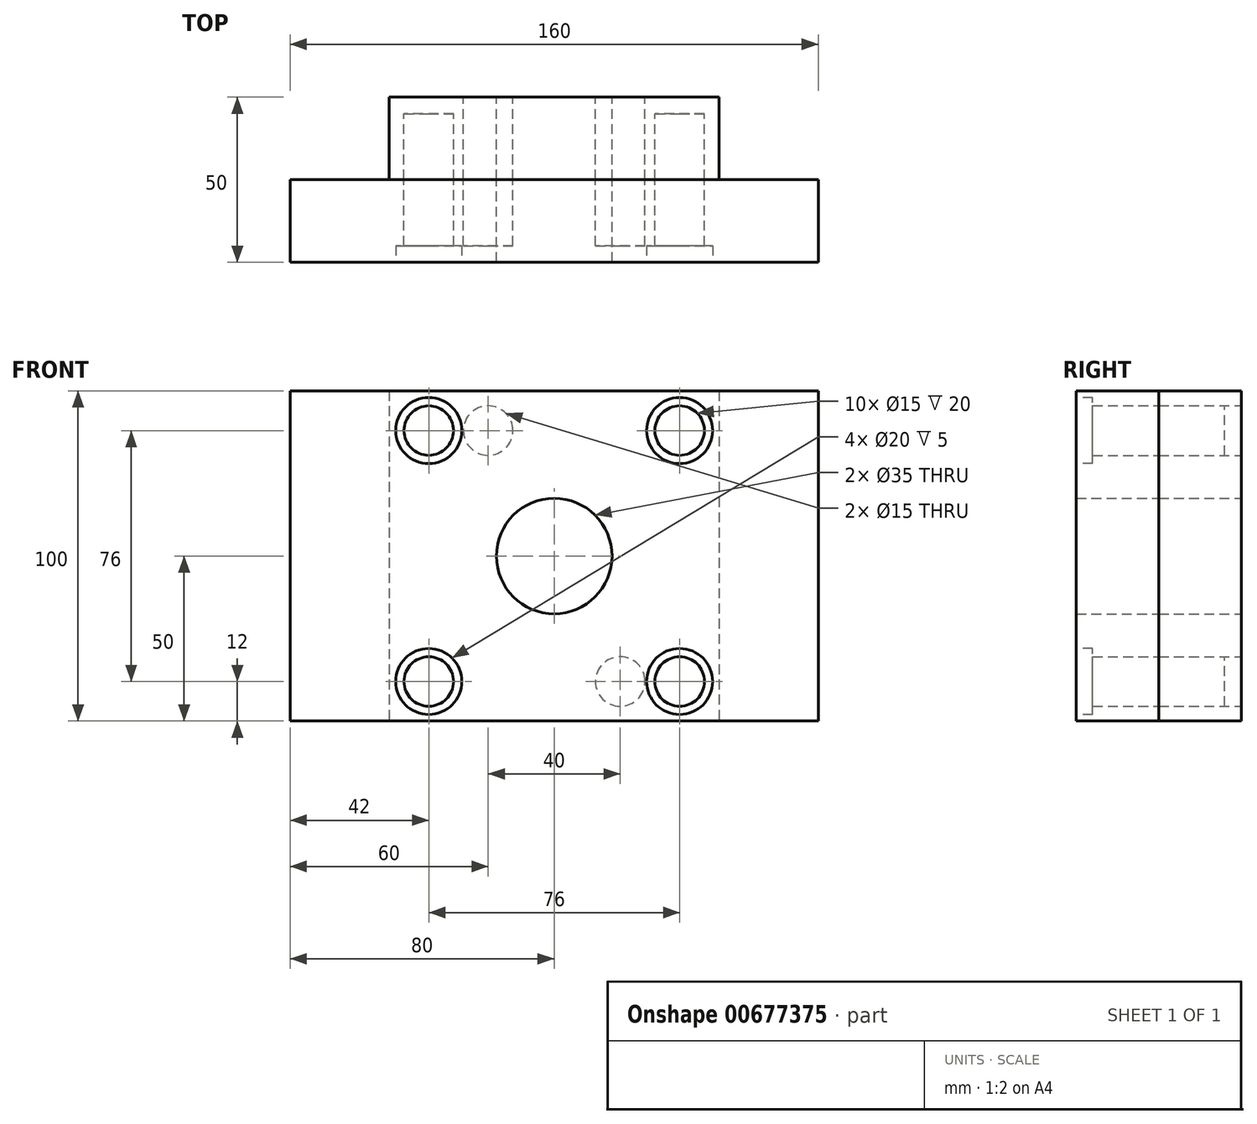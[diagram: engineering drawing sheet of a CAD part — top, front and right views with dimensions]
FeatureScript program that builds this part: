
annotation { "Feature Type Name" : "Feature", "Feature Type Description" : "" }
export const myFeature = defineFeature(function(context is Context, id is Id, definition is map)
    precondition{}
    {
        {
            var Q0;
            Q0=qCreatedBy(makeId("Front.planeOp"),FACE);
            var sketch = newSketch(context, id + "F0", { "sketchPlane" : qUnion([Q0])});
            skLineSegment(sketch, "E0.bottom", {"start": v(50, 50) * mm, "end": v(-50, 50) * mm});
            skLineSegment(sketch, "E0.top", {"start": v(50, -50) * mm, "end": v(-50, -50) * mm});
            skLineSegment(sketch, "E0.left", {"start": v(50, 50) * mm, "end": v(50, -50) * mm});
            skLineSegment(sketch, "E0.right", {"start": v(-50, 50) * mm, "end": v(-50, -50) * mm});
            skPoint(sketch, "E0.middle", {"position": v(0, 0) * mm});
            skCircle(sketch, "E1", {"center": v(0, 0) * mm, "radius": 17.5 * mm});
            skCircle(sketch, "E2", {"center": v(38, 38) * mm, "radius": 7.5 * mm});
            skCircle(sketch, "E3.1.0", {"center": v(-38, 38) * mm, "radius": 7.5 * mm});
            skCircle(sketch, "E3.2.0", {"center": v(-38, -38) * mm, "radius": 7.5 * mm});
            skCircle(sketch, "E3.3.0", {"center": v(38, -38) * mm, "radius": 7.5 * mm});
            skCircle(sketch, "E4", {"center": v(20, -38) * mm, "radius": 7.5 * mm});
            skCircle(sketch, "E5", {"center": v(-20, 38) * mm, "radius": 7.5 * mm});
            skSolve(sketch);
        }
        {
            var Q0;
            Q0 = qSketchRegion(id + "F0", true);
            extrude(context, id + "F1", {"entities" : qUnion([Q0]), "depth" : 25 * mm, "offsetDistance" : 25 * mm});
        }
        {
            var Q0;
            Q0=makeQuery(id+"F1.opExtrude","CAP_FACE",FACE,{"disambiguationData":[OSD([sQuery(id+"F0.wireOp",EDGE,"E0.bottom"),sQuery(id+"F0.wireOp",EDGE,"E0.top"),sQuery(id+"F0.wireOp",EDGE,"E0.left"),sQuery(id+"F0.wireOp",EDGE,"E0.right"),sQuery(id+"F0.wireOp",EDGE,"E1"),sQuery(id+"F0.wireOp",EDGE,"E2"),sQuery(id+"F0.wireOp",EDGE,"E3.1.0"),sQuery(id+"F0.wireOp",EDGE,"E3.2.0"),sQuery(id+"F0.wireOp",EDGE,"E3.3.0"),sQuery(id+"F0.wireOp",EDGE,"E4"),sQuery(id+"F0.wireOp",EDGE,"E5")])],"isStart":false});
            var sketch = newSketch(context, id + "F2", { "sketchPlane" : qUnion([Q0])});
            skLineSegment(sketch, "E6.bottom", {"start": v(80, 50) * mm, "end": v(-80, 50) * mm});
            skLineSegment(sketch, "E6.top", {"start": v(80, -50) * mm, "end": v(-80, -50) * mm});
            skLineSegment(sketch, "E6.left", {"start": v(80, 50) * mm, "end": v(80, -50) * mm});
            skLineSegment(sketch, "E6.right", {"start": v(-80, 50) * mm, "end": v(-80, -50) * mm});
            skPoint(sketch, "E6.middle", {"position": v(0, 0) * mm});
            skCircle(sketch, "E7.0", {"center": v(-38, 38) * mm, "radius": 7.5 * mm});
            skCircle(sketch, "E8.0", {"center": v(-20, 38) * mm, "radius": 7.5 * mm});
            skCircle(sketch, "E9.0", {"center": v(38, 38) * mm, "radius": 7.5 * mm});
            skCircle(sketch, "E10.0", {"center": v(38, -38) * mm, "radius": 7.5 * mm});
            skCircle(sketch, "E11.0", {"center": v(20, -38) * mm, "radius": 7.5 * mm});
            skCircle(sketch, "E12.0", {"center": v(-38, -38) * mm, "radius": 7.5 * mm});
            skCircle(sketch, "E13.0", {"center": v(0, 0) * mm, "radius": 17.5 * mm});
            skSolve(sketch);
        }
        {
            var Q0;
            Q0 = qSketchRegion(id + "F2", true);
            extrude(context, id + "F3", {"entities" : qUnion([Q0]), "depth" : 25 * mm, "offsetDistance" : 25 * mm});
        }
        {
            var Q0;
            Q0=makeQuery(id+"F3.opExtrude","CAP_FACE",FACE,{"disambiguationData":[OSD([sQuery(id+"F2.wireOp",EDGE,"E6.bottom"),sQuery(id+"F2.wireOp",EDGE,"E6.top"),sQuery(id+"F2.wireOp",EDGE,"E6.left"),sQuery(id+"F2.wireOp",EDGE,"E6.right"),sQuery(id+"F2.wireOp",EDGE,"E7.0"),sQuery(id+"F2.wireOp",EDGE,"E8.0"),sQuery(id+"F2.wireOp",EDGE,"E9.0"),sQuery(id+"F2.wireOp",EDGE,"E10.0"),sQuery(id+"F2.wireOp",EDGE,"E11.0"),sQuery(id+"F2.wireOp",EDGE,"E12.0"),sQuery(id+"F2.wireOp",EDGE,"E13.0")])],"isStart":false});
            var sketch = newSketch(context, id + "F4", { "sketchPlane" : qUnion([Q0])});
            skCircle(sketch, "E14.0", {"center": v(-20, 38) * mm, "radius": 7.5 * mm});
            skCircle(sketch, "E15.0", {"center": v(20, -38) * mm, "radius": 7.5 * mm});
            skSolve(sketch);
        }
        {
            var Q0;
            Q0 = qSketchRegion(id + "F4", true);
            extrude(context, id + "F5", {"entities" : qUnion([Q0]), "operationType" : NewBodyOperationType.ADD, "oppositeDirection" : true, "depth" : 5 * mm, "offsetDistance" : 25 * mm});
        }
        {
            var Q0;
            Q0=makeQuery(id+"F1.opExtrude","CAP_FACE",FACE,{"disambiguationData":[OSD([sQuery(id+"F0.wireOp",EDGE,"E0.bottom"),sQuery(id+"F0.wireOp",EDGE,"E0.top"),sQuery(id+"F0.wireOp",EDGE,"E0.left"),sQuery(id+"F0.wireOp",EDGE,"E0.right"),sQuery(id+"F0.wireOp",EDGE,"E1"),sQuery(id+"F0.wireOp",EDGE,"E2"),sQuery(id+"F0.wireOp",EDGE,"E3.1.0"),sQuery(id+"F0.wireOp",EDGE,"E3.2.0"),sQuery(id+"F0.wireOp",EDGE,"E3.3.0"),sQuery(id+"F0.wireOp",EDGE,"E4"),sQuery(id+"F0.wireOp",EDGE,"E5")])],"isStart":true});
            var sketch = newSketch(context, id + "F6", { "sketchPlane" : qUnion([Q0])});
            skCircle(sketch, "E16.0", {"center": v(38, -38) * mm, "radius": 7.5 * mm});
            skCircle(sketch, "E17.0", {"center": v(-38, -38) * mm, "radius": 7.5 * mm});
            skCircle(sketch, "E18.0", {"center": v(-38, 38) * mm, "radius": 7.5 * mm});
            skCircle(sketch, "E19.0", {"center": v(38, 38) * mm, "radius": 7.5 * mm});
            skSolve(sketch);
        }
        {
            var Q0;
            Q0 = qSketchRegion(id + "F6", true);
            extrude(context, id + "F7", {"entities" : qUnion([Q0]), "operationType" : NewBodyOperationType.ADD, "oppositeDirection" : true, "depth" : 5 * mm, "offsetDistance" : 25 * mm});
        }
        {
            var Q0;
            Q0=makeQuery(id+"F5.boolean.opBoolean","MERGE",FACE,{"derivedFrom":[makeQuery(id+"F3.opExtrude","CAP_FACE",FACE,{"disambiguationData":[OSD([sQuery(id+"F2.wireOp",EDGE,"E6.bottom"),sQuery(id+"F2.wireOp",EDGE,"E6.top"),sQuery(id+"F2.wireOp",EDGE,"E6.left"),sQuery(id+"F2.wireOp",EDGE,"E6.right"),sQuery(id+"F2.wireOp",EDGE,"E7.0"),sQuery(id+"F2.wireOp",EDGE,"E8.0"),sQuery(id+"F2.wireOp",EDGE,"E9.0"),sQuery(id+"F2.wireOp",EDGE,"E10.0"),sQuery(id+"F2.wireOp",EDGE,"E11.0"),sQuery(id+"F2.wireOp",EDGE,"E12.0"),sQuery(id+"F2.wireOp",EDGE,"E13.0")])],"isStart":false}),makeQuery(id+"F5.opExtrude","CAP_FACE",FACE,{"disambiguationData":[OSD([sQuery(id+"F4.wireOp",EDGE,"E14.0")])],"isStart":true}),makeQuery(id+"F5.opExtrude","CAP_FACE",FACE,{"disambiguationData":[OSD([sQuery(id+"F4.wireOp",EDGE,"E15.0")])],"isStart":true})]});
            var sketch = newSketch(context, id + "F8", { "sketchPlane" : qUnion([Q0])});
            skCircle(sketch, "E20.0", {"center": v(38, 38) * mm, "radius": 7.5 * mm});
            skCircle(sketch, "E21.0", {"center": v(-38, 38) * mm, "radius": 7.5 * mm});
            skCircle(sketch, "E22.0", {"center": v(-38, -38) * mm, "radius": 7.5 * mm});
            skCircle(sketch, "E23.0", {"center": v(38, -38) * mm, "radius": 7.5 * mm});
            skCircle(sketch, "E24", {"center": v(38, -38) * mm, "radius": 10 * mm});
            skCircle(sketch, "E25.1.0", {"center": v(38, 38) * mm, "radius": 10 * mm});
            skCircle(sketch, "E25.2.0", {"center": v(-38, 38) * mm, "radius": 10 * mm});
            skCircle(sketch, "E25.3.0", {"center": v(-38, -38) * mm, "radius": 10 * mm});
            skPoint(sketch, "E25.center", {"position": v(0, 0) * mm});
            skSolve(sketch);
        }
        {
            var Q0;
            Q0 = qSketchRegion(id + "F8", true);
            extrude(context, id + "F9", {"entities" : qUnion([Q0]), "operationType" : NewBodyOperationType.REMOVE, "oppositeDirection" : true, "depth" : 5 * mm, "offsetDistance" : 25 * mm});
        }
    });
